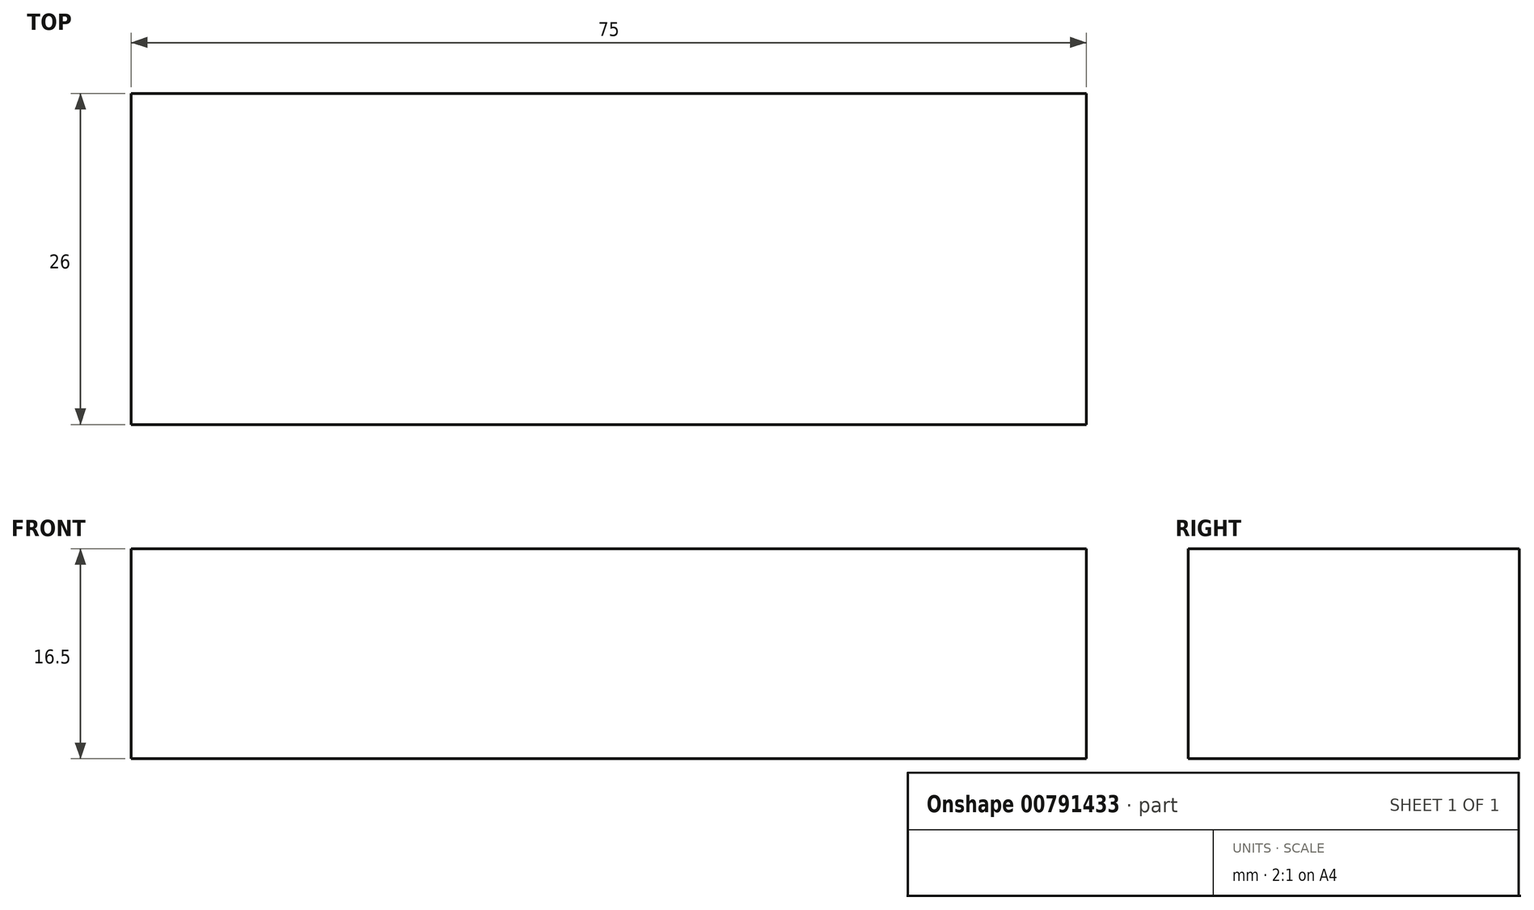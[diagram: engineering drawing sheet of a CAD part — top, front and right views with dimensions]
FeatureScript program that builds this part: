
annotation { "Feature Type Name" : "Feature", "Feature Type Description" : "" }
export const myFeature = defineFeature(function(context is Context, id is Id, definition is map)
    precondition{}
    {
        {
            var Q0;
            Q0=qCreatedBy(makeId("Top.planeOp"),FACE);
            var sketch = newSketch(context, id + "F0", { "sketchPlane" : qUnion([Q0])});
            skLineSegment(sketch, "E0.bottom", {"start": v(0, 0) * mm, "end": v(75, 0) * mm});
            skLineSegment(sketch, "E0.top", {"start": v(0, -26) * mm, "end": v(75, -26) * mm});
            skLineSegment(sketch, "E0.left", {"start": v(0, 0) * mm, "end": v(0, -26) * mm});
            skLineSegment(sketch, "E0.right", {"start": v(75, 0) * mm, "end": v(75, -26) * mm});
            skSolve(sketch);
        }
        {
            var Q0;
            Q0=makeQuery(id+"F0.imprint","IMPRINT",FACE,{"disambiguationData":[TD([[makeQuery(id+"F0.imprint","IMPRINT",EDGE,{"derivedFrom":sQuery(id+"F0.wireOp",EDGE,"E0.bottom")}),-1.0]])]});
            extrude(context, id + "F1", {"entities" : qUnion([Q0]), "depth" : 16.5 * mm, "offsetDistance" : 25 * mm});
        }
    });
